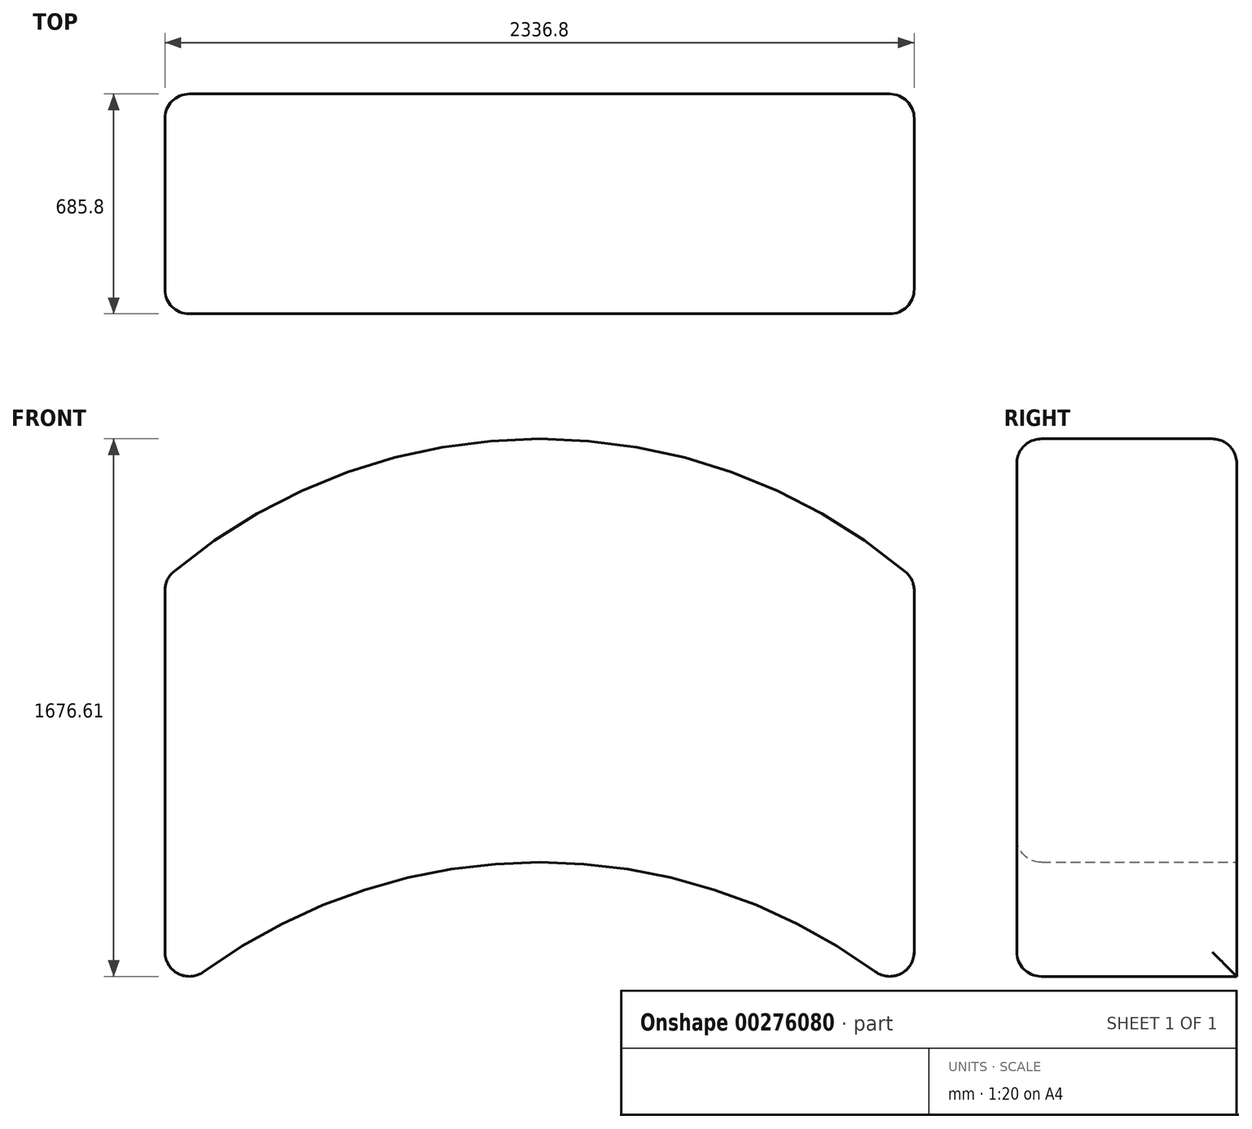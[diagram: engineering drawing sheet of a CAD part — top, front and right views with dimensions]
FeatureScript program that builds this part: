
annotation { "Feature Type Name" : "Feature", "Feature Type Description" : "" }
export const myFeature = defineFeature(function(context is Context, id is Id, definition is map)
    precondition{}
    {
        {
            var Q0;
            Q0=qCreatedBy(makeId("Front.planeOp"),FACE);
            var sketch = newSketch(context, id + "F0", { "sketchPlane" : qUnion([Q0])});
            skLineSegment(sketch, "E0", {"start": v(0, 0) * mm, "end": v(1168.4, 0) * mm});
            skLineSegment(sketch, "E1", {"start": v(0, 0) * mm, "end": v(-1168.4, 0) * mm});
            skLineSegment(sketch, "E2", {"start": v(-1168.4, 0) * mm, "end": v(-1168.4, 1320.8) * mm});
            skLineSegment(sketch, "E3", {"start": v(1168.4, 0) * mm, "end": v(1168.4, 1320.8) * mm});
            skArc(sketch, "E4", {"start": v(1168.4, 1320.8) * mm, "mid": v(0, 1758.6) * mm, "end": v(-1168.4, 1320.8) * mm});
            skArc(sketch, "E5", {"start": v(1168.4, 0) * mm, "mid": v(0, 437.8) * mm, "end": v(-1168.4, 0) * mm});
            skPoint(sketch, "E6.visualSharp", {"position": v(-1168.4, 1320.8) * mm});
            skLineSegment(sketch, "E6.filletArc", {"start": v(-1168.4, 1320.8) * mm, "end": v(-1168.4, 1320.8) * mm});
            skSolve(sketch);
        }
        {
            var Q0;
            Q0=makeQuery(id+"F0.imprint","IMPRINT",FACE,{"disambiguationData":[TD([[makeQuery(id+"F0.imprint","IMPRINT",EDGE,{"derivedFrom":sQuery(id+"F0.wireOp",EDGE,"E2")}),-1.0]])]});
            extrude(context, id + "F1", {"entities" : qUnion([Q0]), "depth" : 685.8 * mm});
        }
        {
            var Q0;
            Q0=makeQuery(id+"F1.opExtrude","CAP_FACE",FACE,{"disambiguationData":[OSD([sQuery(id+"F0.wireOp",EDGE,"E2"),sQuery(id+"F0.wireOp",EDGE,"E3"),sQuery(id+"F0.wireOp",EDGE,"E4"),sQuery(id+"F0.wireOp",EDGE,"E5")])],"isStart":false});
            var Q1;
            Q1=makeQuery(id+"F1.opExtrude","SWEPT_FACE",FACE,{"disambiguationData":[OSD([sQuery(id+"F0.wireOp",EDGE,"E4")])]});
            var Q2;
            Q2=makeQuery(id+"F1.opExtrude","SWEPT_FACE",FACE,{"disambiguationData":[OSD([sQuery(id+"F0.wireOp",EDGE,"E3")])]});
            var Q3;
            Q3=makeQuery(id+"F1.opExtrude","SWEPT_FACE",FACE,{"disambiguationData":[OSD([sQuery(id+"F0.wireOp",EDGE,"E2")])]});
            fillet(context, id + "F2", {"entities" : qUnion([Q0, Q1, Q2, Q3]), "radius" : 76.2 * mm, "tangentPropagation" : true, "allowEdgeOverflow" : false});
        }
    });
